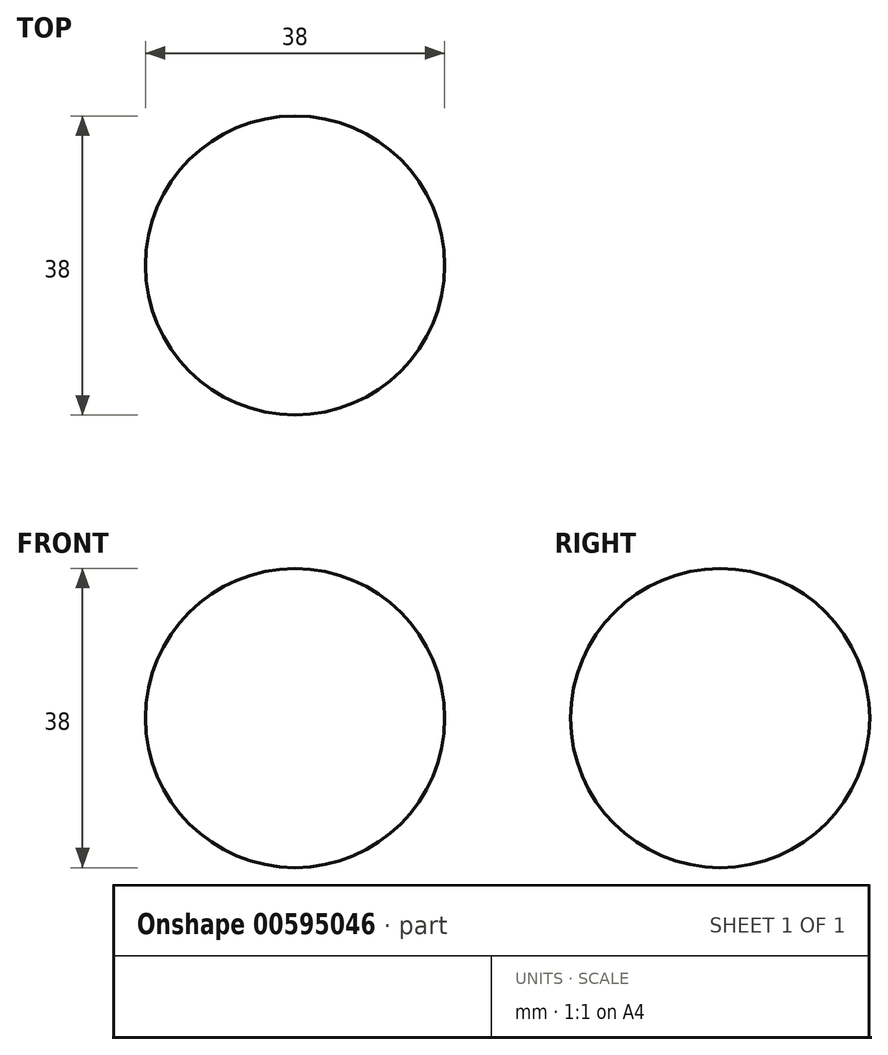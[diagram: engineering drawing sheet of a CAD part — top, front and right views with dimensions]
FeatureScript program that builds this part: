
annotation { "Feature Type Name" : "Feature", "Feature Type Description" : "" }
export const myFeature = defineFeature(function(context is Context, id is Id, definition is map)
    precondition{}
    {
        {
            var Q0;
            Q0=qCreatedBy(makeId("Top.planeOp"),FACE);
            var sketch = newSketch(context, id + "F0", { "sketchPlane" : qUnion([Q0])});
            skCircle(sketch, "E0", {"center": v(0, 0) * mm, "radius": 19 * mm});
            skLineSegment(sketch, "E1", {"start": v(0, -19) * mm, "end": v(0, 19) * mm});
            skSolve(sketch);
        }
        {
            var Q0;
            {var subQ0=sQuery(id+"F0.wireOp",EDGE,"E1");Q0=makeQuery(id+"F0.imprint","IMPRINT",FACE,{"disambiguationData":[TD([[makeQuery(id+"F0.imprint","IMPRINT",EDGE,{"derivedFrom":subQ0}),-1.0]])]});}
            var Q1;
            Q1=sQuery(id+"F0.wireOp",EDGE,"E1");
            revolve(context, id + "F1", {"surfaceOperationType" : NewSurfaceOperationType.NEW, "entities" : qUnion([Q0]), "axis" : qUnion([Q1]), "revolveType" : RevolveType.FULL});
        }
    });
